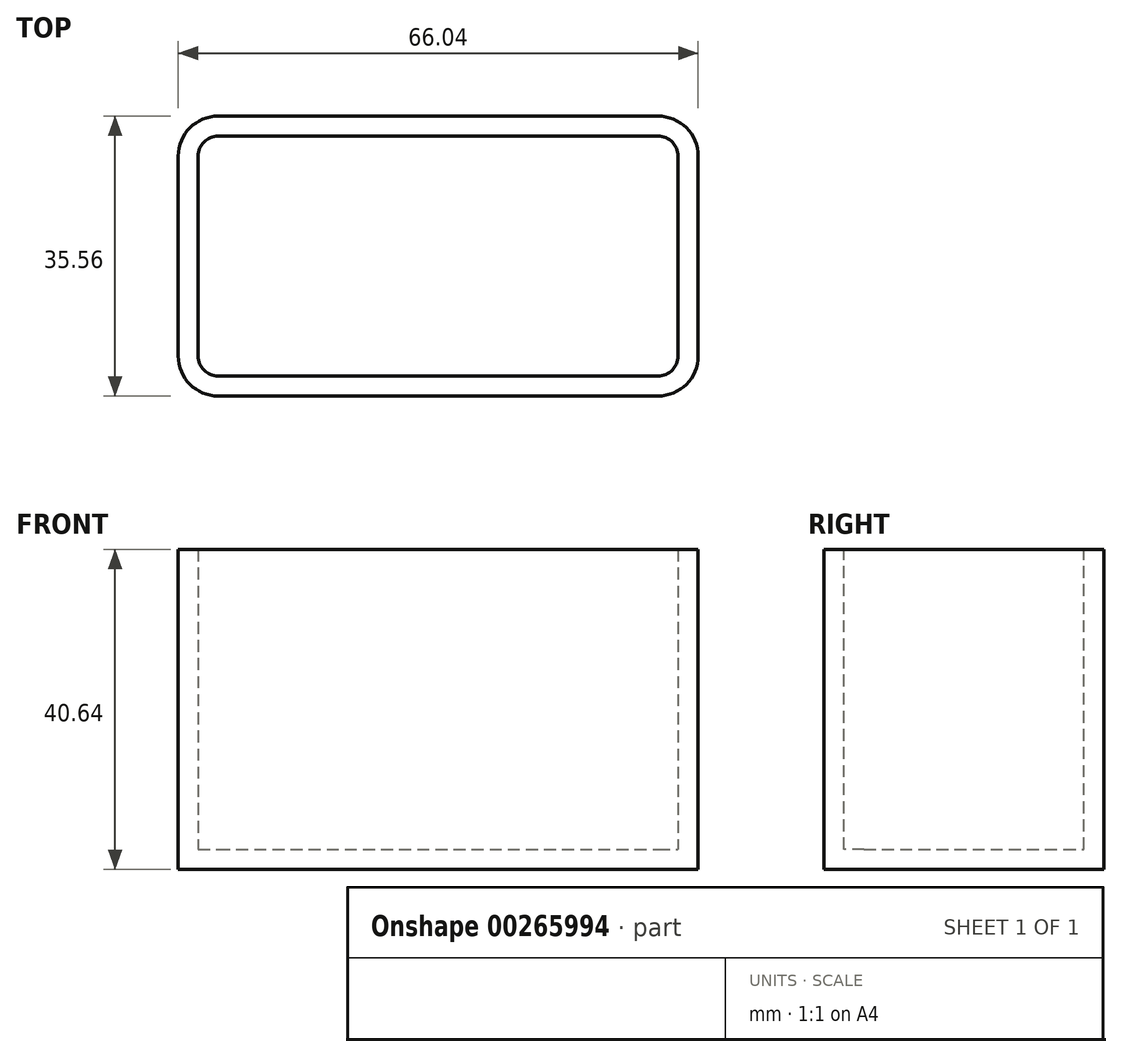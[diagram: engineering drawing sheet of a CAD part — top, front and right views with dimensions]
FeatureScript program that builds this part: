
annotation { "Feature Type Name" : "Feature", "Feature Type Description" : "" }
export const myFeature = defineFeature(function(context is Context, id is Id, definition is map)
    precondition{}
    {
        {
            var Q0;
            Q0=qCreatedBy(makeId("Front.planeOp"),FACE);
            var sketch = newSketch(context, id + "F0", { "sketchPlane" : qUnion([Q0])});
            skLineSegment(sketch, "E0.bottom", {"start": v(-33.02, 20.32) * mm, "end": v(33.02, 20.32) * mm});
            skLineSegment(sketch, "E0.top", {"start": v(-33.02, -20.32) * mm, "end": v(33.02, -20.32) * mm});
            skLineSegment(sketch, "E0.left", {"start": v(-33.02, 20.32) * mm, "end": v(-33.02, -20.32) * mm});
            skLineSegment(sketch, "E0.right", {"start": v(33.02, 20.32) * mm, "end": v(33.02, -20.32) * mm});
            skPoint(sketch, "E0.middle", {"position": v(0, 0) * mm});
            skSolve(sketch);
        }
        {
            var Q0;
            Q0 = qSketchRegion(id + "F0", true);
            extrude(context, id + "F1", {"entities" : qUnion([Q0]), "depth" : 35.56 * mm});
        }
        {
            var Q0;
            Q0=makeQuery(id+"F1.opExtrude","CAP_EDGE",EDGE,{"disambiguationData":[OSD([sQuery(id+"F0.wireOp",EDGE,"E0.right")])],"isStart":false});
            var Q1;
            Q1=makeQuery(id+"F1.opExtrude","CAP_EDGE",EDGE,{"disambiguationData":[OSD([sQuery(id+"F0.wireOp",EDGE,"E0.right")])],"isStart":true});
            var Q2;
            Q2=makeQuery(id+"F1.opExtrude","CAP_EDGE",EDGE,{"disambiguationData":[OSD([sQuery(id+"F0.wireOp",EDGE,"E0.left")])],"isStart":false});
            var Q3;
            Q3=makeQuery(id+"F1.opExtrude","CAP_EDGE",EDGE,{"disambiguationData":[OSD([sQuery(id+"F0.wireOp",EDGE,"E0.left")])],"isStart":true});
            fillet(context, id + "F2", {"entities" : qUnion([Q0, Q1, Q2, Q3]), "radius" : 5.08 * mm, "tangentPropagation" : true, "allowEdgeOverflow" : false});
        }
        {
            var Q0;
            Q0=makeQuery(id+"F1.opExtrude","SWEPT_FACE",FACE,{"disambiguationData":[OSD([sQuery(id+"F0.wireOp",EDGE,"E0.bottom")])]});
            shell(context, id + "F3", {"entities" : qUnion([Q0]), "thickness" : 2.54 * mm});
        }
    });
